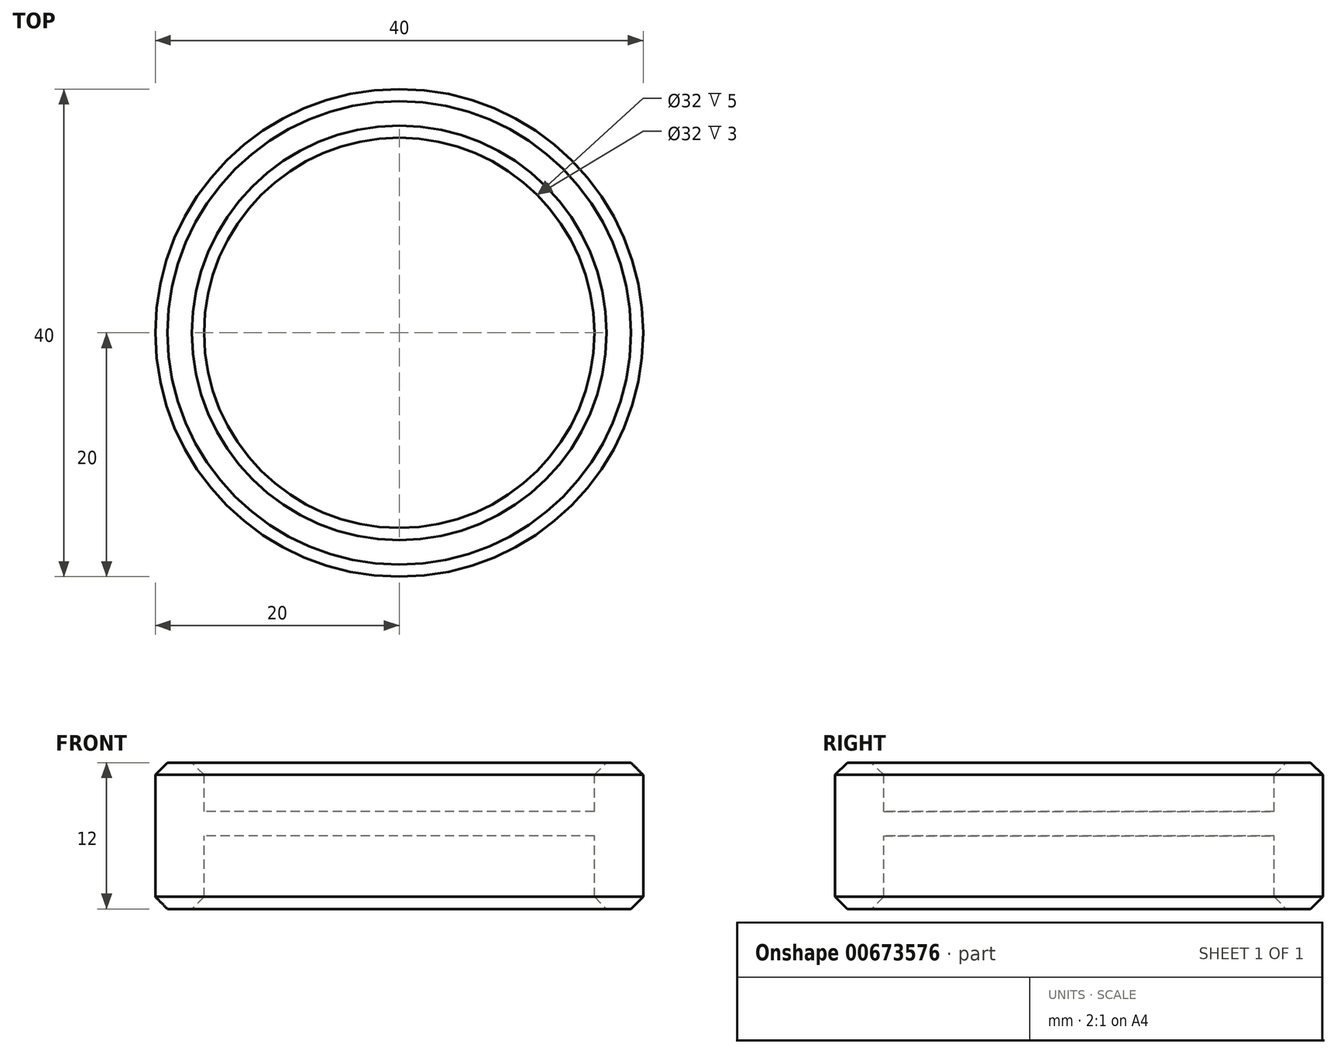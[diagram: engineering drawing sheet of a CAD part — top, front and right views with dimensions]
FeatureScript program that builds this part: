
annotation { "Feature Type Name" : "Feature", "Feature Type Description" : "" }
export const myFeature = defineFeature(function(context is Context, id is Id, definition is map)
    precondition{}
    {
        {
            var Q0;
            Q0=qCreatedBy(makeId("Right.planeOp"),FACE);
            var sketch = newSketch(context, id + "F0", { "sketchPlane" : qUnion([Q0])});
            skLineSegment(sketch, "E0", {"start": v(0, 15.84) * mm, "end": v(0, -19.11) * mm, "construction": true});
            skLineSegment(sketch, "E1", {"start": v(-20, 4.18) * mm, "end": v(-20, -7.82) * mm});
            skLineSegment(sketch, "E2", {"start": v(-20, -7.82) * mm, "end": v(-16, -7.82) * mm});
            skLineSegment(sketch, "E3", {"start": v(-16, -7.82) * mm, "end": v(-16, -1.82) * mm});
            skLineSegment(sketch, "E4", {"start": v(-16, -1.82) * mm, "end": v(0, -1.82) * mm});
            skLineSegment(sketch, "E5", {"start": v(0, -1.82) * mm, "end": v(0, 0.18) * mm});
            skLineSegment(sketch, "E6", {"start": v(0, 0.18) * mm, "end": v(-16, 0.18) * mm});
            skLineSegment(sketch, "E7", {"start": v(-16, 0.18) * mm, "end": v(-16, 4.18) * mm});
            skLineSegment(sketch, "E8", {"start": v(-16, 4.18) * mm, "end": v(-20, 4.18) * mm});
            skSolve(sketch);
        }
        {
            var Q0;
            Q0=makeQuery(id+"F0.imprint","IMPRINT",FACE,{"disambiguationData":[TD([[makeQuery(id+"F0.imprint","IMPRINT",EDGE,{"derivedFrom":sQuery(id+"F0.wireOp",EDGE,"E1")}),1.0]])]});
            var Q1;
            Q1=sQuery(id+"F0.wireOp",EDGE,"E0");
            revolve(context, id + "F1", {"entities" : qUnion([Q0]), "axis" : qUnion([Q1]), "revolveType" : RevolveType.FULL});
        }
        {
            var Q0;
            Q0=makeQuery(id+"F1.opRevolve","SWEPT_EDGE",EDGE,{"disambiguationData":[OSD([sQuery(id+"F0.wireOp",EDGE,"E7"),sQuery(id+"F0.wireOp",EDGE,"E8")])]});
            var Q1;
            Q1=makeQuery(id+"F1.opRevolve","SWEPT_EDGE",EDGE,{"disambiguationData":[OSD([sQuery(id+"F0.wireOp",EDGE,"E1"),sQuery(id+"F0.wireOp",EDGE,"E8")])]});
            var Q2;
            Q2=makeQuery(id+"F1.opRevolve","SWEPT_EDGE",EDGE,{"disambiguationData":[OSD([sQuery(id+"F0.wireOp",EDGE,"E1"),sQuery(id+"F0.wireOp",EDGE,"E2")])]});
            var Q3;
            Q3=makeQuery(id+"F1.opRevolve","SWEPT_EDGE",EDGE,{"disambiguationData":[OSD([sQuery(id+"F0.wireOp",EDGE,"E2"),sQuery(id+"F0.wireOp",EDGE,"E3")])]});
            chamfer(context, id + "F2", {"entities" : qUnion([Q0, Q1, Q2, Q3]), "width" : 1 * mm, "tangentPropagation" : true});
        }
    });
